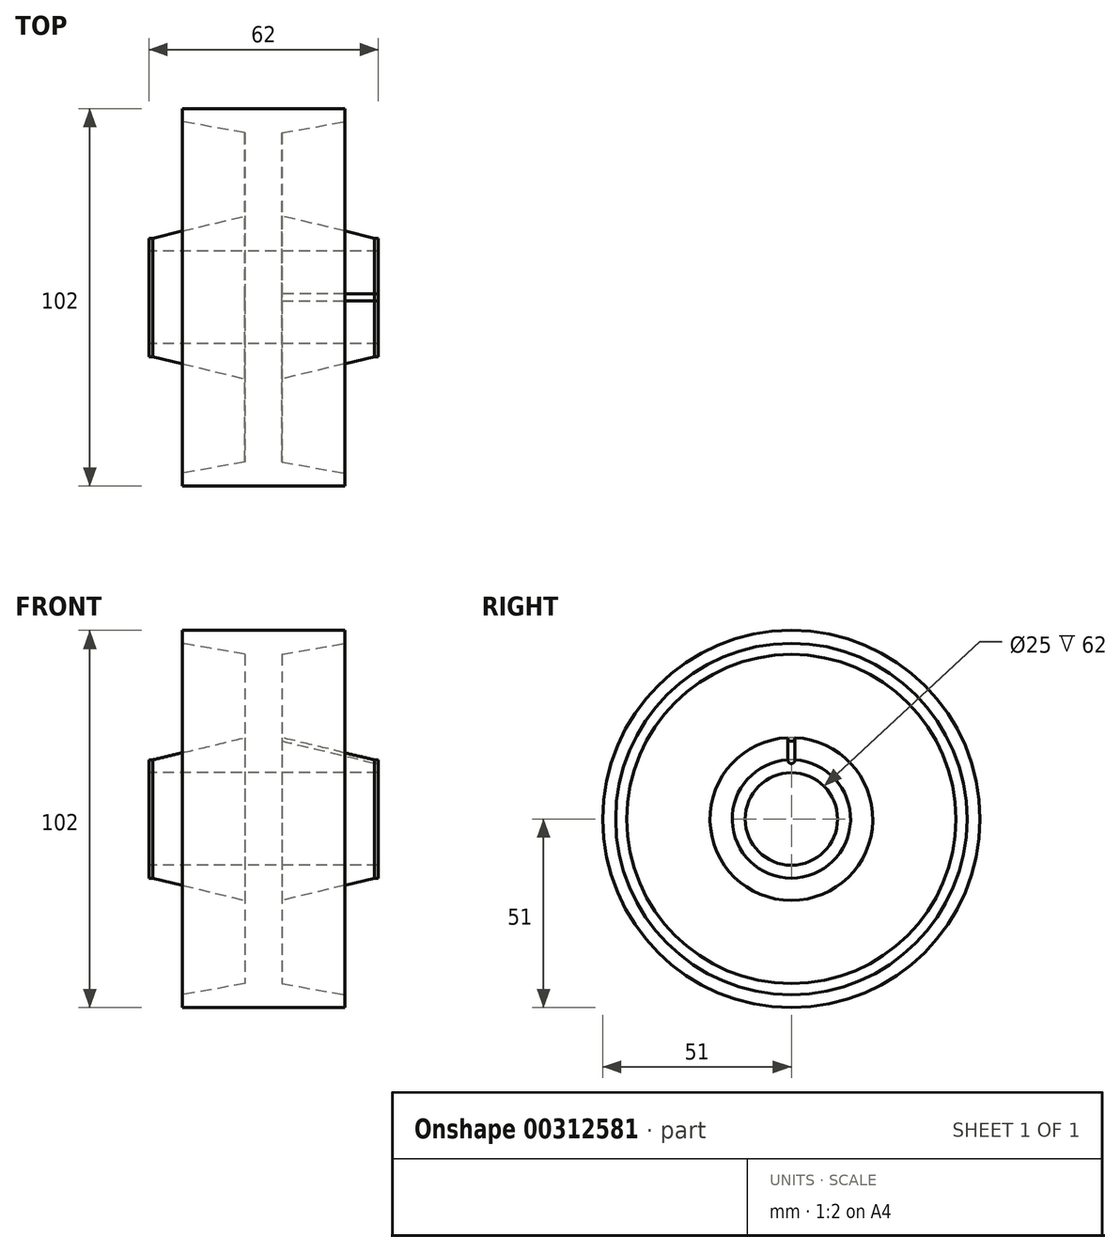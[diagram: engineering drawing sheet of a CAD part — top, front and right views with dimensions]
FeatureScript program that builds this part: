
annotation { "Feature Type Name" : "Feature", "Feature Type Description" : "" }
export const myFeature = defineFeature(function(context is Context, id is Id, definition is map)
    precondition{}
    {
        {
            var Q0;
            Q0=qCreatedBy(makeId("Front.planeOp"),FACE);
            var sketch = newSketch(context, id + "F0", { "sketchPlane" : qUnion([Q0])});
            skLineSegment(sketch, "E0", {"start": v(0, 51) * mm, "end": v(22, 51) * mm});
            skLineSegment(sketch, "E1", {"start": v(22, 51) * mm, "end": v(22, 47.5) * mm});
            skLineSegment(sketch, "E2", {"start": v(22, 47.5) * mm, "end": v(5, 44.5) * mm});
            skLineSegment(sketch, "E3", {"start": v(5, 44.5) * mm, "end": v(5, 22) * mm});
            skLineSegment(sketch, "E4", {"start": v(5, 22) * mm, "end": v(30, 16) * mm});
            skLineSegment(sketch, "E5", {"start": v(0, 56.38) * mm, "end": v(0, -19.66) * mm, "construction": true});
            skLineSegment(sketch, "E6", {"start": v(30, 16) * mm, "end": v(30, 12.5) * mm});
            skLineSegment(sketch, "E7", {"start": v(30, 12.5) * mm, "end": v(0, 12.5) * mm});
            skLineSegment(sketch, "E8.MirrorCS", {"start": v(-30, 16) * mm, "end": v(-30, 12.5) * mm});
            skLineSegment(sketch, "E9.MirrorCS", {"start": v(-22, 51) * mm, "end": v(-22, 47.5) * mm});
            skLineSegment(sketch, "E10.MirrorCS", {"start": v(-22, 47.5) * mm, "end": v(-5, 44.5) * mm});
            skLineSegment(sketch, "E11.MirrorCS", {"start": v(-5, 22) * mm, "end": v(-30, 16) * mm});
            skLineSegment(sketch, "E12.MirrorCS", {"start": v(-5, 44.5) * mm, "end": v(-5, 22) * mm});
            skLineSegment(sketch, "E13.MirrorCS", {"start": v(0, 51) * mm, "end": v(-22, 51) * mm});
            skLineSegment(sketch, "E14.MirrorCS", {"start": v(-30, 12.5) * mm, "end": v(0, 12.5) * mm});
            skLineSegment(sketch, "E15", {"start": v(-34.97, 0) * mm, "end": v(39.27, 0) * mm, "construction": true});
            skSolve(sketch);
        }
        {
            var Q0;
            Q0=makeQuery(id+"F0.imprint","IMPRINT",FACE,{"disambiguationData":[TD([[makeQuery(id+"F0.imprint","IMPRINT",EDGE,{"derivedFrom":sQuery(id+"F0.wireOp",EDGE,"E0")}),-1.0]])]});
            var Q1;
            Q1=sQuery(id+"F0.wireOp",EDGE,"E15");
            revolve(context, id + "F1", {"entities" : qUnion([Q0]), "axis" : qUnion([Q1]), "revolveType" : RevolveType.FULL});
        }
        {
            var Q0;
            Q0=makeQuery(id+"F1.opRevolve","SWEPT_FACE",FACE,{"disambiguationData":[OSD([sQuery(id+"F0.wireOp",EDGE,"E6")])]});
            var sketch = newSketch(context, id + "F2", { "sketchPlane" : qUnion([Q0])});
            skCircle(sketch, "E16", {"center": v(0, 16) * mm, "radius": 1 * mm});
            skSolve(sketch);
        }
        {
            var Q0;
            Q0=qCreatedBy(makeId("Front.planeOp"),FACE);
            var sketch = newSketch(context, id + "F3", { "sketchPlane" : qUnion([Q0])});
            skLineSegment(sketch, "E17", {"start": v(30, 16) * mm, "end": v(5, 22) * mm});
            skPoint(sketch, "E18.0", {"position": v(30, 16) * mm});
            skSolve(sketch);
        }
        {
            var Q0;
            Q0=makeQuery(id+"F1.opRevolve","SWEPT_FACE",FACE,{"disambiguationData":[OSD([sQuery(id+"F0.wireOp",EDGE,"E3")])]});
            var sketch = newSketch(context, id + "F4", { "sketchPlane" : qUnion([Q0])});
            skPoint(sketch, "E19.0", {"position": v(0, 22) * mm});
            skCircle(sketch, "E20", {"center": v(0, 22) * mm, "radius": 1 * mm});
            skSolve(sketch);
        }
        {
            var Q1;
            Q1 = qSketchRegion(id + "F2", true);
            var Q2;
            Q2 = qSketchRegion(id + "F4", true);
            loft(context, id + "F5", {"operationType" : NewBodyOperationType.REMOVE, "sheetProfilesArray" : [{ "sheetProfileEntities" : qUnion([Q1]) }, { "sheetProfileEntities" : qUnion([Q2]) }]});
        }
        {
            var Q0;
            Q0=makeQuery(id+"F1.opRevolve","SWEPT_FACE",FACE,{"disambiguationData":[OSD([sQuery(id+"F0.wireOp",EDGE,"E6")])]});
            extrude(context, id + "F6", {"entities" : qUnion([Q0]), "operationType" : NewBodyOperationType.ADD, "depth" : 1 * mm});
        }
        {
            var Q0;
            Q0=makeQuery(id+"F1.opRevolve","SWEPT_FACE",FACE,{"disambiguationData":[OSD([sQuery(id+"F0.wireOp",EDGE,"E8.MirrorCS")])]});
            extrude(context, id + "F7", {"entities" : qUnion([Q0]), "operationType" : NewBodyOperationType.ADD, "depth" : 1 * mm});
        }
    });
